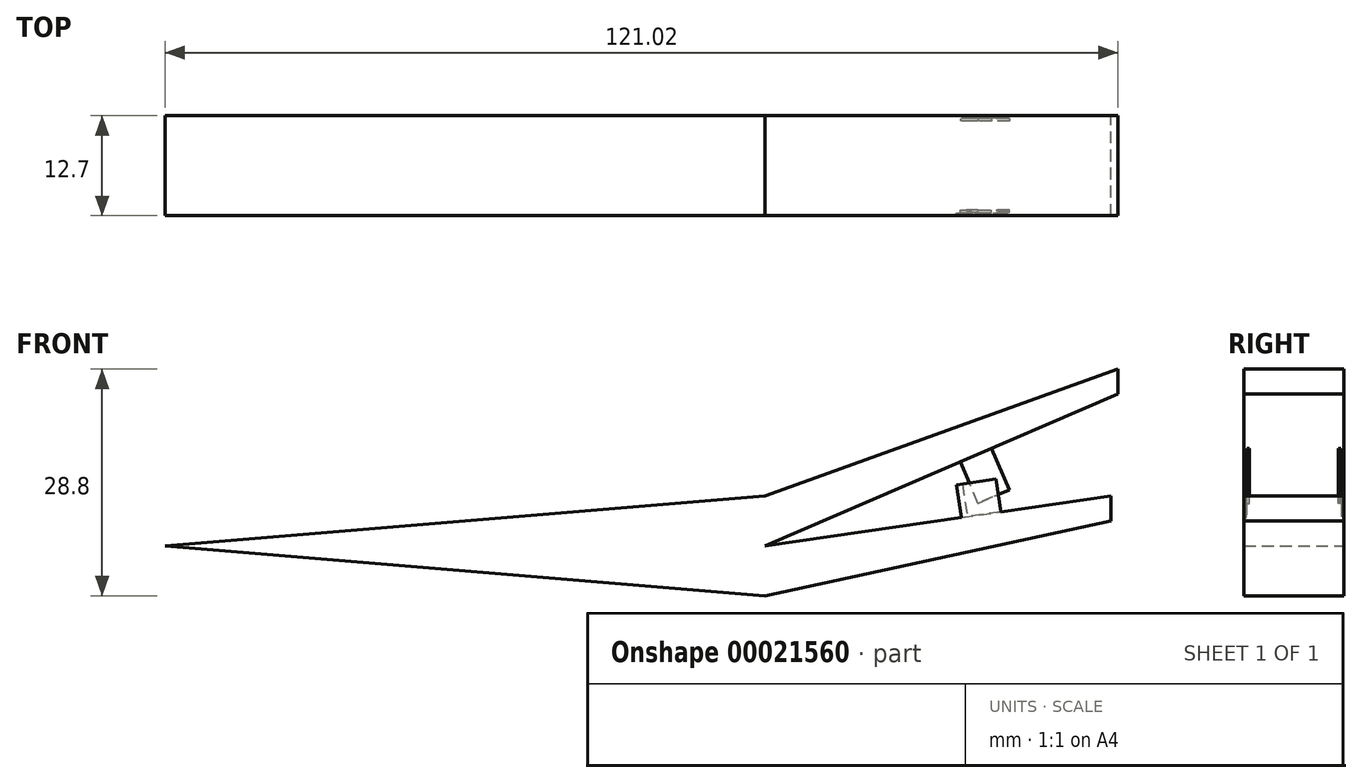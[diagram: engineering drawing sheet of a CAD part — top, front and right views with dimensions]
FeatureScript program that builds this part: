
annotation { "Feature Type Name" : "Feature", "Feature Type Description" : "" }
export const myFeature = defineFeature(function(context is Context, id is Id, definition is map)
    precondition{}
    {
        {
            var Q0;
            Q0=qCreatedBy(makeId("Front.planeOp"),FACE);
            var sketch = newSketch(context, id + "F0", { "sketchPlane" : qUnion([Q0])});
            skLineSegment(sketch, "E0", {"start": v(-34.8, 0.8) * mm, "end": v(41.4, 0.8) * mm});
            skLineSegment(sketch, "E1", {"start": v(41.4, 7.16) * mm, "end": v(41.4, -5.54) * mm});
            skLineSegment(sketch, "E2", {"start": v(-34.8, 0.8) * mm, "end": v(41.4, 7.16) * mm});
            skLineSegment(sketch, "E3", {"start": v(-34.8, 0.8) * mm, "end": v(41.4, -5.54) * mm});
            skLineSegment(sketch, "E4", {"start": v(86.22, 23.26) * mm, "end": v(86.22, 20.09) * mm});
            skLineSegment(sketch, "E5", {"start": v(41.4, 7.16) * mm, "end": v(86.22, 23.26) * mm});
            skLineSegment(sketch, "E6", {"start": v(41.4, 0.8) * mm, "end": v(86.22, 20.09) * mm});
            skLineSegment(sketch, "E7", {"start": v(85.37, 7.16) * mm, "end": v(85.37, 3.98) * mm});
            skLineSegment(sketch, "E8", {"start": v(41.4, 0.8) * mm, "end": v(85.37, 7.16) * mm});
            skLineSegment(sketch, "E9", {"start": v(41.4, -5.54) * mm, "end": v(85.37, 3.98) * mm});
            skSolve(sketch);
        }
        {
            var Q0;
            Q0 = qSketchRegion(id + "F0", true);
            extrude(context, id + "F1", {"entities" : qUnion([Q0]), "depth" : 12.7 * mm});
        }
        {
            var Q0;
            Q0=makeQuery(id+"F1.opExtrude","SWEPT_FACE",FACE,{"disambiguationData":[OSD([sQuery(id+"F0.wireOp",EDGE,"E8")])]});
            var sketch = newSketch(context, id + "F2", { "sketchPlane" : qUnion([Q0])});
            skLineSegment(sketch, "E10.bottom", {"start": v(66.28, -12.7) * mm, "end": v(71.35, -12.7) * mm});
            skLineSegment(sketch, "E10.top", {"start": v(66.28, -12.38) * mm, "end": v(71.35, -12.38) * mm});
            skLineSegment(sketch, "E10.left", {"start": v(66.28, -12.7) * mm, "end": v(66.28, -12.38) * mm});
            skLineSegment(sketch, "E10.right", {"start": v(71.35, -12.7) * mm, "end": v(71.35, -12.38) * mm});
            skLineSegment(sketch, "E11.bottom", {"start": v(67.03, 0) * mm, "end": v(71.35, 0) * mm});
            skLineSegment(sketch, "E11.top", {"start": v(67.03, 0) * mm, "end": v(71.35, 0) * mm});
            skLineSegment(sketch, "E11.left", {"start": v(67.03, 0) * mm, "end": v(67.03, 0) * mm});
            skLineSegment(sketch, "E11.right", {"start": v(71.35, 0) * mm, "end": v(71.35, 0) * mm});
            skLineSegment(sketch, "E12", {"start": v(71.35, -12.38) * mm, "end": v(71.35, 0) * mm});
            skLineSegment(sketch, "E13.bottom", {"start": v(71.35, 0) * mm, "end": v(67.03, 0) * mm});
            skLineSegment(sketch, "E13.top", {"start": v(71.35, -0.32) * mm, "end": v(67.03, -0.32) * mm});
            skLineSegment(sketch, "E13.left", {"start": v(71.35, 0) * mm, "end": v(71.35, -0.32) * mm});
            skLineSegment(sketch, "E13.right", {"start": v(67.03, 0) * mm, "end": v(67.03, -0.32) * mm});
            skSolve(sketch);
        }
        {
            var Q0;
            Q0=makeQuery(id+"F1.opExtrude","SWEPT_FACE",FACE,{"disambiguationData":[OSD([sQuery(id+"F0.wireOp",EDGE,"E6")])]});
            var sketch = newSketch(context, id + "F3", { "sketchPlane" : qUnion([Q0])});
            skLineSegment(sketch, "E14.bottom", {"start": v(69.67, 0.35) * mm, "end": v(65.35, 0.35) * mm});
            skLineSegment(sketch, "E14.top", {"start": v(69.67, 0.66) * mm, "end": v(65.35, 0.66) * mm});
            skLineSegment(sketch, "E14.left", {"start": v(69.67, 0.35) * mm, "end": v(69.67, 0.66) * mm});
            skLineSegment(sketch, "E14.right", {"start": v(65.35, 0.35) * mm, "end": v(65.35, 0.66) * mm});
            skLineSegment(sketch, "E15", {"start": v(65.35, 12.7) * mm, "end": v(65.35, 12.3) * mm});
            skLineSegment(sketch, "E16.bottom", {"start": v(65.35, 12.3) * mm, "end": v(69.67, 12.3) * mm});
            skLineSegment(sketch, "E16.top", {"start": v(65.35, 11.98) * mm, "end": v(69.67, 11.98) * mm});
            skLineSegment(sketch, "E16.left", {"start": v(65.35, 12.3) * mm, "end": v(65.35, 11.98) * mm});
            skLineSegment(sketch, "E16.right", {"start": v(69.67, 12.3) * mm, "end": v(69.67, 11.98) * mm});
            skSolve(sketch);
        }
        {
            var Q0;
            Q0 = qSketchRegion(id + "F3", true);
            extrude(context, id + "F4", {"entities" : qUnion([Q0]), "operationType" : NewBodyOperationType.ADD, "depth" : 5.7 * mm});
        }
        {
            var Q0;
            Q0 = qSketchRegion(id + "F2", true);
            extrude(context, id + "F5", {"entities" : qUnion([Q0]), "operationType" : NewBodyOperationType.ADD, "depth" : 4.2 * mm});
        }
    });
